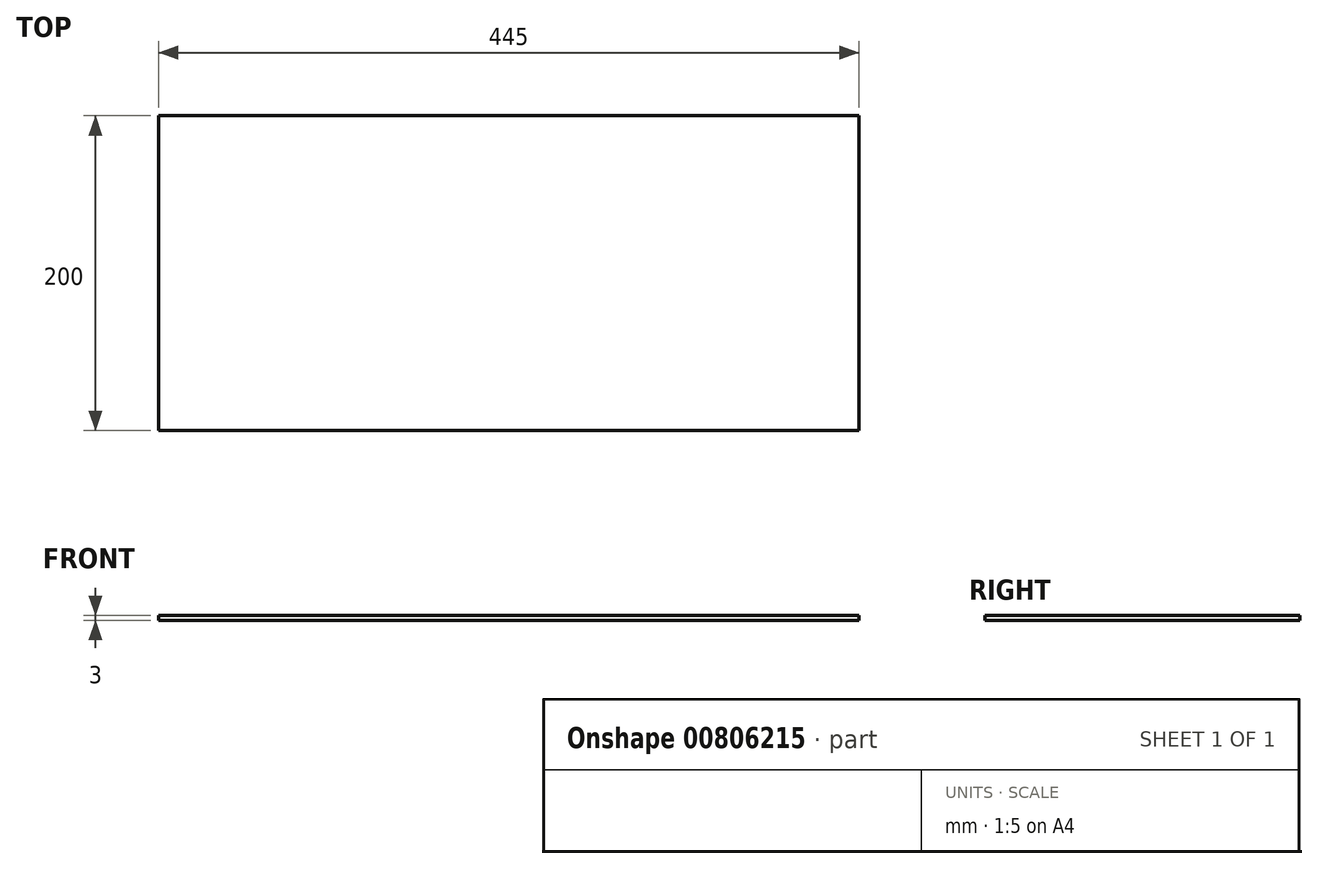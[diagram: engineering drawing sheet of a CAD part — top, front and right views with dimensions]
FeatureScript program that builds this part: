
annotation { "Feature Type Name" : "Feature", "Feature Type Description" : "" }
export const myFeature = defineFeature(function(context is Context, id is Id, definition is map)
    precondition{}
    {
        {
            var Q0;
            Q0=qCreatedBy(makeId("Top.planeOp"),FACE);
            var sketch = newSketch(context, id + "F0", { "sketchPlane" : qUnion([Q0])});
            skLineSegment(sketch, "E0.bottom", {"start": v(222.5, -100) * mm, "end": v(-222.5, -100) * mm});
            skLineSegment(sketch, "E0.top", {"start": v(222.5, 100) * mm, "end": v(-222.5, 100) * mm});
            skLineSegment(sketch, "E0.left", {"start": v(222.5, -100) * mm, "end": v(222.5, 100) * mm});
            skLineSegment(sketch, "E0.right", {"start": v(-222.5, -100) * mm, "end": v(-222.5, 100) * mm});
            skPoint(sketch, "E0.middle", {"position": v(0, 0) * mm});
            skSolve(sketch);
        }
        {
            var Q0;
            Q0=qSketchRegion(id+"F0",true);
            extrude(context, id + "F1", {"entities" : qUnion([Q0]), "depth" : 3 * mm, "offsetDistance" : 25 * mm});
        }
    });
